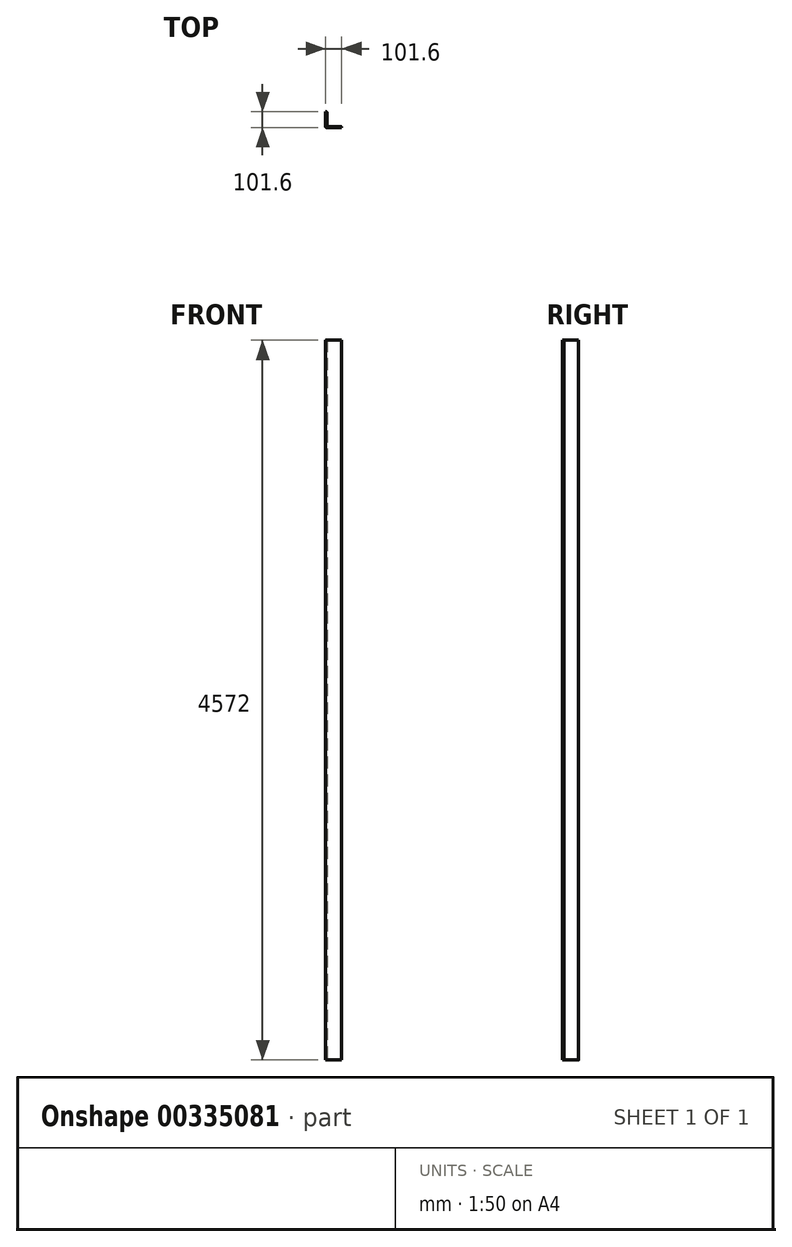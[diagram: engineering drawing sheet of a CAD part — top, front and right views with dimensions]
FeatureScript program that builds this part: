
annotation { "Feature Type Name" : "Feature", "Feature Type Description" : "" }
export const myFeature = defineFeature(function(context is Context, id is Id, definition is map)
    precondition{}
    {
        {
            var Q0;
            Q0=qCreatedBy(makeId("Top.planeOp"),FACE);
            var sketch = newSketch(context, id + "F0", { "sketchPlane" : qUnion([Q0])});
            skLineSegment(sketch, "E0", {"start": v(0, 101.6) * mm, "end": v(0, 0) * mm});
            skLineSegment(sketch, "E1", {"start": v(0, 0) * mm, "end": v(101.6, 0) * mm});
            skLineSegment(sketch, "E2", {"start": v(101.6, 0) * mm, "end": v(101.6, 7.94) * mm});
            skLineSegment(sketch, "E3", {"start": v(101.6, 7.94) * mm, "end": v(7.94, 7.94) * mm});
            skLineSegment(sketch, "E4", {"start": v(7.94, 7.94) * mm, "end": v(7.94, 101.6) * mm});
            skLineSegment(sketch, "E5", {"start": v(7.94, 101.6) * mm, "end": v(0, 101.6) * mm});
            skSolve(sketch);
        }
        {
            var Q0;
            Q0=makeQuery(id+"F0.imprint","IMPRINT",FACE,{"disambiguationData":[TD([[makeQuery(id+"F0.imprint","IMPRINT",EDGE,{"derivedFrom":sQuery(id+"F0.wireOp",EDGE,"E0")}),1.0]])]});
            extrude(context, id + "F1", {"entities" : qUnion([Q0]), "depth" : 4572 * mm});
        }
        {
            var Q0;
            Q0=makeQuery(id+"F1.opExtrude","SWEPT_EDGE",EDGE,{"disambiguationData":[OSD([sQuery(id+"F0.wireOp",EDGE,"E4"),sQuery(id+"F0.wireOp",EDGE,"E5")])]});
            var Q1;
            Q1=makeQuery(id+"F1.opExtrude","SWEPT_EDGE",EDGE,{"disambiguationData":[OSD([sQuery(id+"F0.wireOp",EDGE,"E2"),sQuery(id+"F0.wireOp",EDGE,"E3")])]});
            var Q2;
            Q2=makeQuery(id+"F1.opExtrude","SWEPT_EDGE",EDGE,{"disambiguationData":[OSD([sQuery(id+"F0.wireOp",EDGE,"E0"),sQuery(id+"F0.wireOp",EDGE,"E1")])]});
            var Q3;
            Q3=makeQuery(id+"F1.opExtrude","SWEPT_EDGE",EDGE,{"disambiguationData":[OSD([sQuery(id+"F0.wireOp",EDGE,"E3"),sQuery(id+"F0.wireOp",EDGE,"E4")])]});
            fillet(context, id + "F2", {"entities" : qUnion([Q0, Q1, Q2, Q3]), "radius" : 5 * mm, "tangentPropagation" : true, "allowEdgeOverflow" : false});
        }
    });
